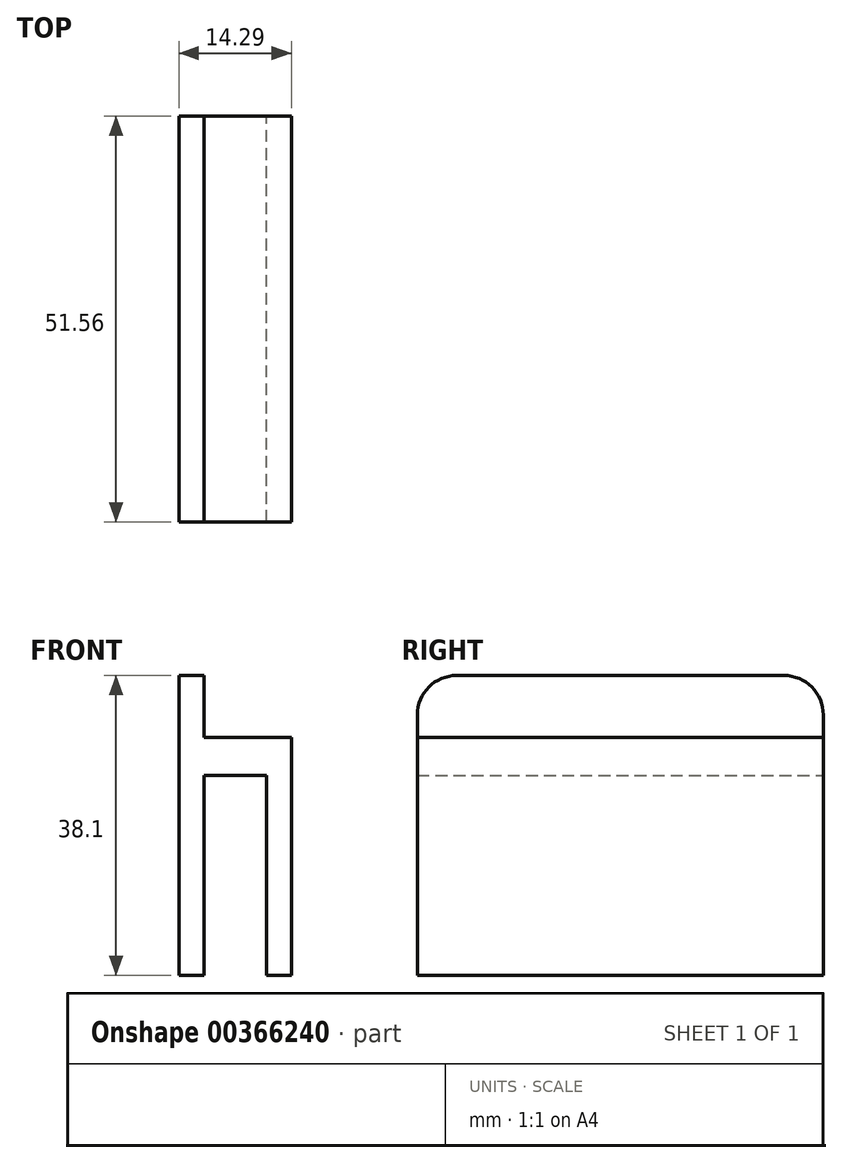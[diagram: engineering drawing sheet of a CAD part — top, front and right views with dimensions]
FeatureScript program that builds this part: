
annotation { "Feature Type Name" : "Feature", "Feature Type Description" : "" }
export const myFeature = defineFeature(function(context is Context, id is Id, definition is map)
    precondition{}
    {
        {
            var Q0;
            Q0=qCreatedBy(makeId("Front.planeOp"),FACE);
            var sketch = newSketch(context, id + "F0", { "sketchPlane" : qUnion([Q0])});
            skLineSegment(sketch, "E0", {"start": v(0, 0) * mm, "end": v(-3.18, 0) * mm});
            skLineSegment(sketch, "E1", {"start": v(-3.18, 0) * mm, "end": v(-3.18, 25.4) * mm});
            skLineSegment(sketch, "E2", {"start": v(-3.18, 25.4) * mm, "end": v(-11.11, 25.4) * mm});
            skLineSegment(sketch, "E3", {"start": v(-11.11, 25.4) * mm, "end": v(-11.11, 0) * mm});
            skLineSegment(sketch, "E4", {"start": v(-11.11, 0) * mm, "end": v(-14.29, 0) * mm});
            skLineSegment(sketch, "E5", {"start": v(-14.29, 0) * mm, "end": v(-14.29, 38.1) * mm});
            skLineSegment(sketch, "E6", {"start": v(-14.29, 38.1) * mm, "end": v(-11.11, 38.1) * mm});
            skLineSegment(sketch, "E7", {"start": v(-11.11, 38.1) * mm, "end": v(-11.11, 30.25) * mm});
            skLineSegment(sketch, "E8", {"start": v(-3.97, 30.25) * mm, "end": v(-11.11, 30.25) * mm});
            skLineSegment(sketch, "E9", {"start": v(-3.97, 30.25) * mm, "end": v(0, 30.25) * mm});
            skLineSegment(sketch, "E10", {"start": v(0, 30.25) * mm, "end": v(0, 0) * mm});
            skSolve(sketch);
        }
        {
            var Q0;
            Q0=makeQuery(id+"F0.imprint","IMPRINT",FACE,{"disambiguationData":[TD([[makeQuery(id+"F0.imprint","IMPRINT",EDGE,{"derivedFrom":sQuery(id+"F0.wireOp",EDGE,"E0")}),-1.0]])]});
            extrude(context, id + "F1", {"entities" : qUnion([Q0]), "depth" : 51.56 * mm});
        }
        {
            var Q0;
            Q0=makeQuery(id+"F1.opExtrude","CAP_EDGE",EDGE,{"disambiguationData":[OSD([sQuery(id+"F0.wireOp",EDGE,"E6")])],"isStart":false});
            var Q1;
            Q1=makeQuery(id+"F1.opExtrude","CAP_EDGE",EDGE,{"disambiguationData":[OSD([sQuery(id+"F0.wireOp",EDGE,"E6")])],"isStart":true});
            fillet(context, id + "F2", {"entities" : qUnion([Q0, Q1]), "radius" : 5 * mm, "tangentPropagation" : true, "allowEdgeOverflow" : false});
        }
    });
